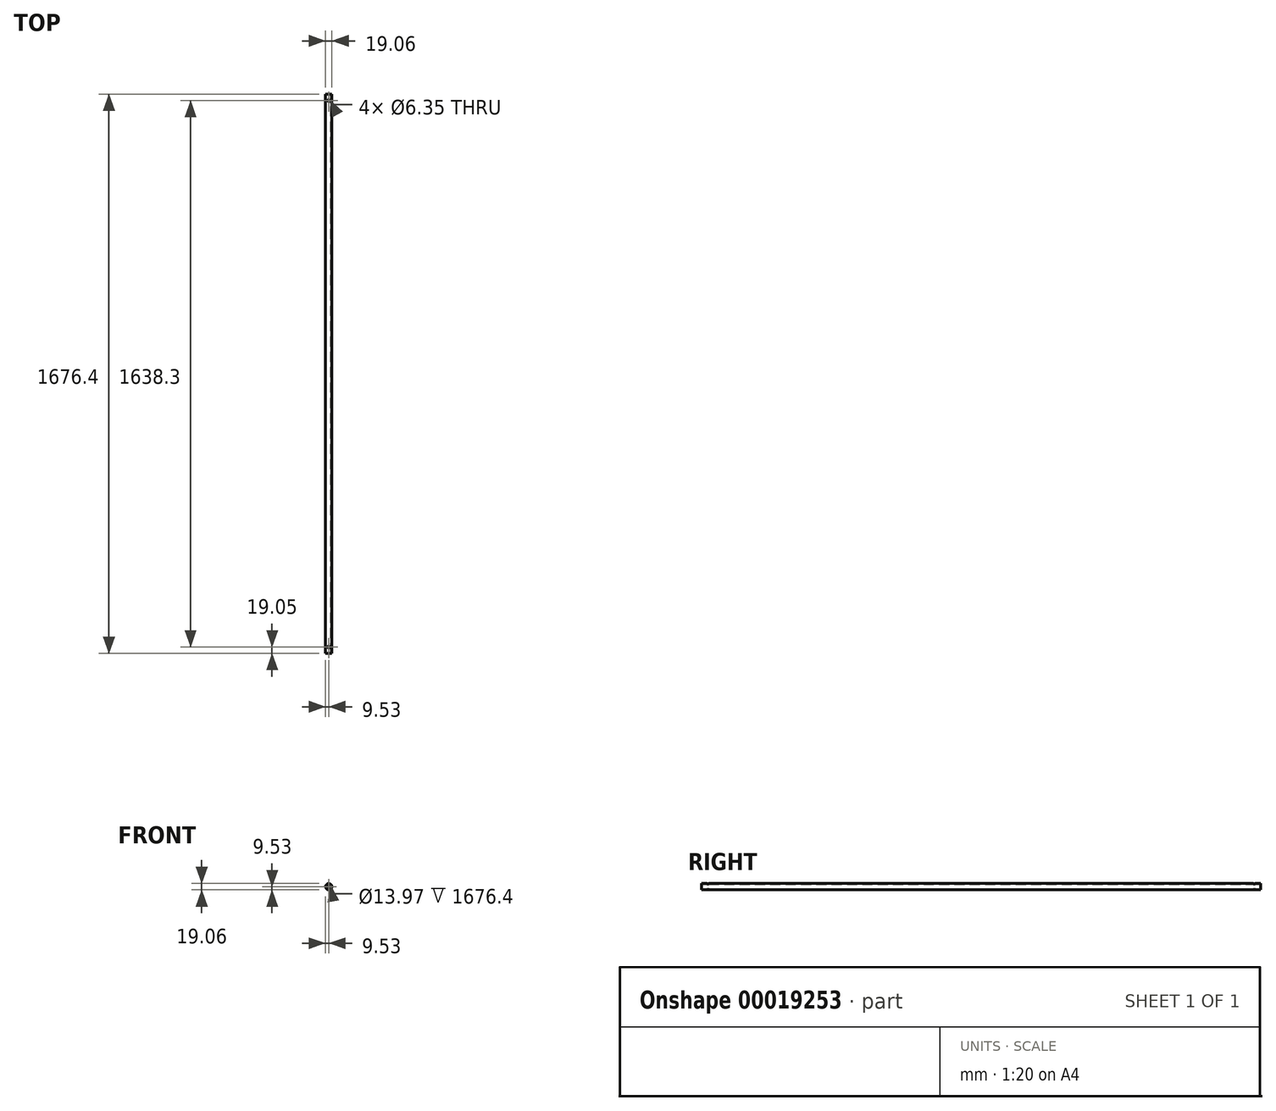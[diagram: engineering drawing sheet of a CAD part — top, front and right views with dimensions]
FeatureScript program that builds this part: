
annotation { "Feature Type Name" : "Feature", "Feature Type Description" : "" }
export const myFeature = defineFeature(function(context is Context, id is Id, definition is map)
    precondition{}
    {
        {
            var Q0;
            Q0=qCreatedBy(makeId("Front.planeOp"),FACE);
            var sketch = newSketch(context, id + "F0", { "sketchPlane" : qUnion([Q0])});
            skCircle(sketch, "E0", {"center": v(0, 0) * mm, "radius": 9.53 * mm});
            skSolve(sketch);
        }
        {
            var Q0;
            Q0=makeQuery(id+"F0.imprint","IMPRINT",FACE,{"disambiguationData":[TD([[makeQuery(id+"F0.imprint","IMPRINT",EDGE,{"derivedFrom":sQuery(id+"F0.wireOp",EDGE,"E0")}),1.0]])]});
            extrude(context, id + "F1", {"entities" : qUnion([Q0]), "endBound" : BoundingType.SYMMETRIC, "depth" : 1676.4 * mm});
        }
        {
            var Q0;
            Q0=makeQuery(id+"F1.opExtrude","CAP_FACE",FACE,{"disambiguationData":[OSD([sQuery(id+"F0.wireOp",EDGE,"E0")])],"isStart":false});
            var Q1;
            Q1=makeQuery(id+"F1.opExtrude","CAP_FACE",FACE,{"disambiguationData":[OSD([sQuery(id+"F0.wireOp",EDGE,"E0")])],"isStart":true});
            shell(context, id + "F2", {"entities" : qUnion([Q0, Q1]), "thickness" : 2.54 * mm});
        }
        {
            var Q0;
            Q0=qCreatedBy(makeId("Top.planeOp"),FACE);
            var sketch = newSketch(context, id + "F3", { "sketchPlane" : qUnion([Q0])});
            skCircle(sketch, "E1", {"center": v(0, 819.15) * mm, "radius": 3.18 * mm});
            skCircle(sketch, "E2", {"center": v(0, -819.15) * mm, "radius": 3.18 * mm});
            skLineSegment(sketch, "E3", {"start": v(0, -819.15) * mm, "end": v(0, -838.2) * mm, "construction": true});
            skLineSegment(sketch, "E4", {"start": v(0, 819.15) * mm, "end": v(0, 838.2) * mm, "construction": true});
            skSolve(sketch);
        }
        {
            var Q0;
            Q0 = qSketchRegion(id + "F3", true);
            extrude(context, id + "F4", {"entities" : qUnion([Q0]), "operationType" : NewBodyOperationType.REMOVE, "endBound" : BoundingType.THROUGH_ALL, "oppositeDirection" : true, "depth" : 25.4 * mm, "hasSecondDirection" : true, "secondDirectionBound" : SecondDirectionBoundingType.THROUGH_ALL, "secondDirectionOppositeDirection" : false, "secondDirectionDepth" : 25.4 * mm});
        }
    });
